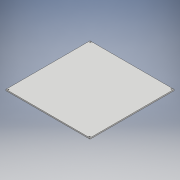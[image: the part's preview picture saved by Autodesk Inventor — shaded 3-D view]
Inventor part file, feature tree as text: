
AUTODESK INVENTOR PART (.ipt)
format: ipt  version: 2017 (Build 210142000, 142)  size: 107,520 bytes
history: native  units: mm
features: extrude x2, sketch x2
ambient origin geometry x8: Origin, YZ Plane, XZ Plane, XY Plane, X Axis, Y Axis, Z Axis, Center Point
bodies: Solid1 (feature_tree)
feature tree (4):
  extrude  "Extrusion1"  Depth=3.0mm TaperAngle=0.0deg
  extrude  "Extrusion3"  Depth=3.0mm
  sketch  "Sketch1"  dims[d0=213.0mm d1=3.0mm d2=0.0mm]
  sketch  "Sketch2"  dims[d3=3.0mm d4=1.0mm d5=2.0mm d8=3.0mm d9=0.0mm]
